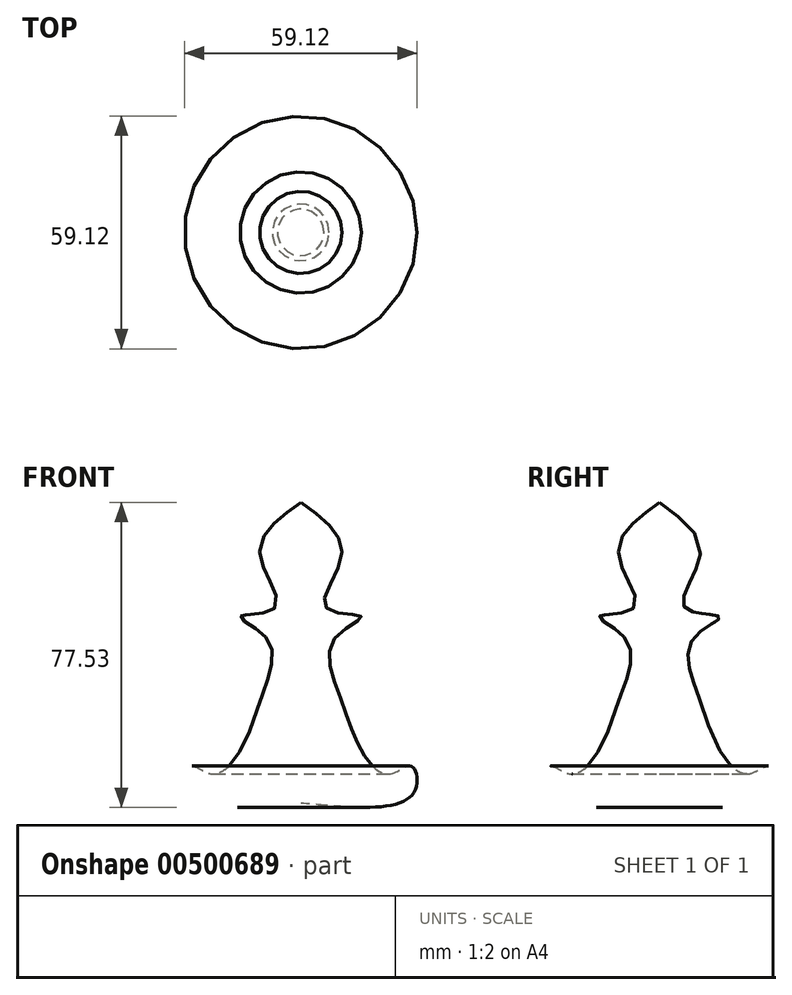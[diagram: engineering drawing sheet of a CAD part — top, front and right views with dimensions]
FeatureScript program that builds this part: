
annotation { "Feature Type Name" : "Feature", "Feature Type Description" : "" }
export const myFeature = defineFeature(function(context is Context, id is Id, definition is map)
    precondition{}
    {
        {
            var Q0;
            Q0=qCreatedBy(makeId("Front.planeOp"),FACE);
            var sketch = newSketch(context, id + "F0", { "sketchPlane" : qUnion([Q0])});
            skLineSegment(sketch, "E0", {"start": v(0, 0) * mm, "end": v(0, 76.46) * mm});
            skFitSpline(sketch, "E1", {"points": [v(0, 76.46) * mm, v(10.4, 63.23) * mm, v(6.38, 49.76) * mm, v(15.36, 47.4) * mm, v(8.5, 41.72) * mm, v(9.93, 27.06) * mm, v(16.07, 12.17) * mm, v(22.7, 7.45) * mm, v(28.13, 9.34) * mm, v(28.6, 2.48) * mm, v(0, 0) * mm], "startDerivative": vector(140.14, -100.54) * mm, "endDerivative": vector(-247.6, 23.54) * mm});
            skSolve(sketch);
        }
        {
            var Q0;
            Q0 = qSketchRegion(id + "F0", true);
            var Q1;
            Q1=sQuery(id+"F0.wireOp",EDGE,"E0");
            revolve(context, id + "F1", {"entities" : qUnion([Q0]), "axis" : qUnion([Q1]), "revolveType" : RevolveType.FULL});
        }
    });
